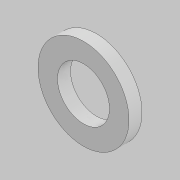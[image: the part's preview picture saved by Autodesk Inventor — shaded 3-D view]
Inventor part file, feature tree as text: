
AUTODESK INVENTOR PART (.ipt)
format: ipt  version: 2021 (Build 250183000, 183)  size: 84,992 bytes
history: native  units: mm
features: extrude x1, sketch x1
ambient origin geometry x8: Origin, YZ Plane, XZ Plane, XY Plane, X Axis, Y Axis, Z Axis, Center Point
bodies: Solid1 (feature_tree)
feature tree (2):
  extrude  "Extrusion1"  Depth=15.0mm
  sketch  "Sketch1"  dims[d0=60.0mm d1=105.0mm d2=15.0mm d3=0.0mm]
